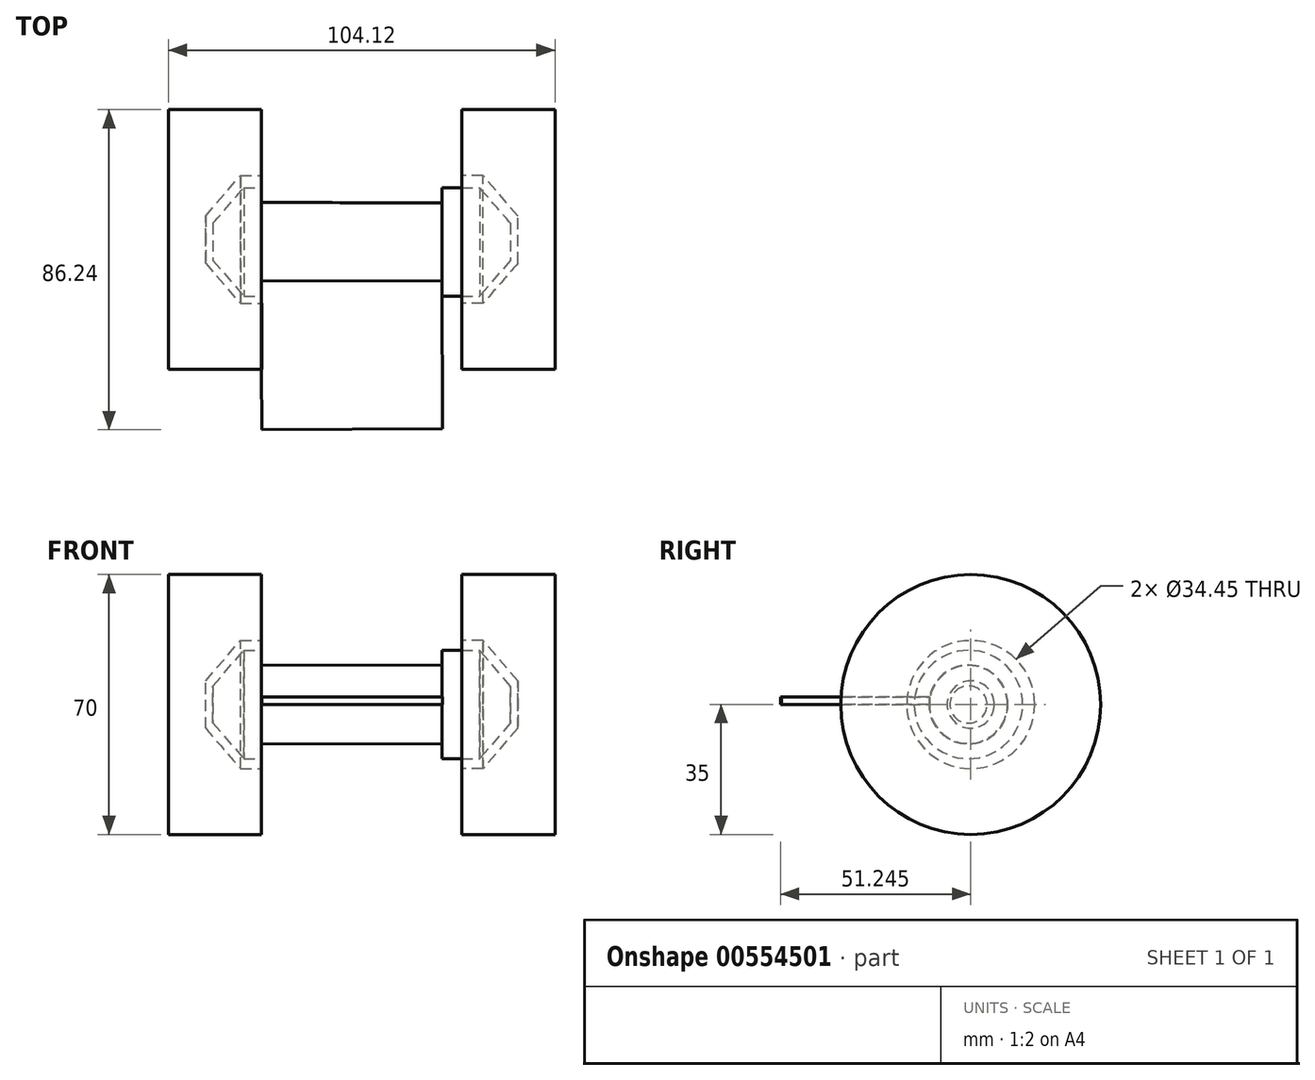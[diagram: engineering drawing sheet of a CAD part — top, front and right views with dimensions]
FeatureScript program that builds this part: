
annotation { "Feature Type Name" : "Feature", "Feature Type Description" : "" }
export const myFeature = defineFeature(function(context is Context, id is Id, definition is map)
    precondition{}
    {
        {
            var Q0;
            Q0=qCreatedBy(makeId("Top.planeOp"),FACE);
            var sketch = newSketch(context, id + "F0", { "sketchPlane" : qUnion([Q0])});
            skLineSegment(sketch, "E0", {"start": v(41.47, 0) * mm, "end": v(-22.03, 0) * mm});
            skLineSegment(sketch, "E1", {"start": v(-22.03, 0) * mm, "end": v(-30.34, 9.6) * mm});
            skLineSegment(sketch, "E2", {"start": v(41.47, 0) * mm, "end": v(49.78, 9.6) * mm});
            skLineSegment(sketch, "E3", {"start": v(-30.34, 9.6) * mm, "end": v(-30.34, 14.6) * mm});
            skLineSegment(sketch, "E4", {"start": v(49.78, 9.6) * mm, "end": v(49.78, 14.6) * mm});
            skLineSegment(sketch, "E5", {"start": v(49.78, 14.6) * mm, "end": v(-30.34, 14.6) * mm});
            skLineSegment(sketch, "E6.0", {"start": v(-32.34, 8.86) * mm, "end": v(-32.34, 15.22) * mm});
            skLineSegment(sketch, "E6.1", {"start": v(51.78, 8.86) * mm, "end": v(51.78, 15.22) * mm});
            skLineSegment(sketch, "E6.2", {"start": v(42.38, -2) * mm, "end": v(51.78, 8.86) * mm});
            skLineSegment(sketch, "E6.3", {"start": v(42.38, -2) * mm, "end": v(-22.94, -2) * mm});
            skLineSegment(sketch, "E6.4", {"start": v(-22.94, -2) * mm, "end": v(-32.34, 8.86) * mm});
            skLineSegment(sketch, "E7", {"start": v(-32.34, 15.22) * mm, "end": v(-42.34, 15.22) * mm});
            skLineSegment(sketch, "E8", {"start": v(-42.34, 15.22) * mm, "end": v(-42.34, -19.78) * mm});
            skLineSegment(sketch, "E9", {"start": v(51.78, 15.22) * mm, "end": v(61.78, 15.22) * mm});
            skLineSegment(sketch, "E10", {"start": v(61.78, 15.22) * mm, "end": v(61.78, -19.78) * mm});
            skLineSegment(sketch, "E11", {"start": v(61.78, -19.78) * mm, "end": v(-42.34, -19.78) * mm});
            skLineSegment(sketch, "E12", {"start": v(-17.15, -2) * mm, "end": v(-17.15, -19.78) * mm});
            skLineSegment(sketch, "E13", {"start": v(61.78, -19.78) * mm, "end": v(36.66, -19.78) * mm});
            skLineSegment(sketch, "E14", {"start": v(61.78, -19.78) * mm, "end": v(40.6, -19.78) * mm});
            skLineSegment(sketch, "E15", {"start": v(40.6, -19.78) * mm, "end": v(36.66, -19.78) * mm});
            skLineSegment(sketch, "E16", {"start": v(36.66, -19.78) * mm, "end": v(36.66, -2) * mm});
            skLineSegment(sketch, "E17", {"start": v(-17.36, 3.98) * mm, "end": v(-17.15, -36.02) * mm});
            skLineSegment(sketch, "E18", {"start": v(-17.15, -36.02) * mm, "end": v(31.51, -35.76) * mm});
            skLineSegment(sketch, "E19", {"start": v(31.51, -35.76) * mm, "end": v(31.3, 4.1) * mm});
            skLineSegment(sketch, "E20", {"start": v(31.3, 4.1) * mm, "end": v(-17.36, 3.98) * mm});
            skSolve(sketch);
        }
        {
            var Q0;
            {var subQ0=sQuery(id+"F0.wireOp",EDGE,"E18");Q0=makeQuery(id+"F0.imprint","IMPRINT",FACE,{"disambiguationData":[TD([[makeQuery(id+"F0.imprint","IMPRINT",EDGE,{"derivedFrom":subQ0}),1.0]])]});}
            var Q1;
            {var subQ0=sQuery(id+"F0.wireOp",EDGE,"E12");Q1=makeQuery(id+"F0.imprint","IMPRINT",FACE,{"disambiguationData":[TD([[makeQuery(id+"F0.imprint","IMPRINT",EDGE,{"derivedFrom":subQ0}),1.0]])]});}
            var Q2;
            {var subQ1=sQuery(id+"F0.wireOp",EDGE,"E0");var subQ6=sQuery(id+"F0.wireOp",EDGE,"E19");var subQ7=makeQuery(id+"F0.imprint","INTERSECT",VERTEX,{"derivedFrom":[subQ1,subQ6]});Q2=makeQuery(id+"F0.imprint","IMPRINT",FACE,{"disambiguationData":[TD([[makeQuery(id+"F0.imprint","IMPRINT",EDGE,{"disambiguationData":[TD([[subQ7,-1.0]])],"derivedFrom":subQ1}),1.0]])]});}
            var Q3;
            {var subQ5=sQuery(id+"F0.wireOp",EDGE,"E20");Q3=makeQuery(id+"F0.imprint","IMPRINT",FACE,{"disambiguationData":[TD([[makeQuery(id+"F0.imprint","IMPRINT",EDGE,{"derivedFrom":subQ5}),1.0]])]});}
            extrude(context, id + "F1", {"entities" : qUnion([Q0, Q1, Q2, Q3]), "depth" : 2 * mm, "offsetDistance" : 25 * mm});
        }
        {
            var Q0;
            Q0=makeQuery(id+"F0.imprint","IMPRINT",FACE,{"disambiguationData":[TD([[makeQuery(id+"F0.imprint","IMPRINT",EDGE,{"derivedFrom":sQuery(id+"F0.wireOp",EDGE,"E0")}),-1.0]])]});
            var Q1;
            Q1=sQuery(id+"F0.wireOp",EDGE,"E5");
            revolve(context, id + "F2", {"entities" : qUnion([Q0]), "axis" : qUnion([Q1]), "revolveType" : RevolveType.FULL});
        }
        {
            var Q0;
            Q0=makeQuery(id+"F0.imprint","IMPRINT",FACE,{"disambiguationData":[TD([[makeQuery(id+"F0.imprint","IMPRINT",EDGE,{"derivedFrom":sQuery(id+"F0.wireOp",EDGE,"E6.0")}),1.0]])]});
            var Q1;
            Q1=sQuery(id+"F0.wireOp",EDGE,"E7");
            revolve(context, id + "F3", {"entities" : qUnion([Q0]), "axis" : qUnion([Q1]), "revolveType" : RevolveType.FULL});
        }
        {
            var Q0;
            Q0=makeQuery(id+"F0.imprint","IMPRINT",FACE,{"disambiguationData":[TD([[makeQuery(id+"F0.imprint","IMPRINT",EDGE,{"derivedFrom":sQuery(id+"F0.wireOp",EDGE,"E6.1")}),-1.0]])]});
            var Q1;
            Q1=sQuery(id+"F0.wireOp",EDGE,"E9");
            revolve(context, id + "F4", {"entities" : qUnion([Q0]), "axis" : qUnion([Q1]), "revolveType" : RevolveType.FULL});
        }
    });
